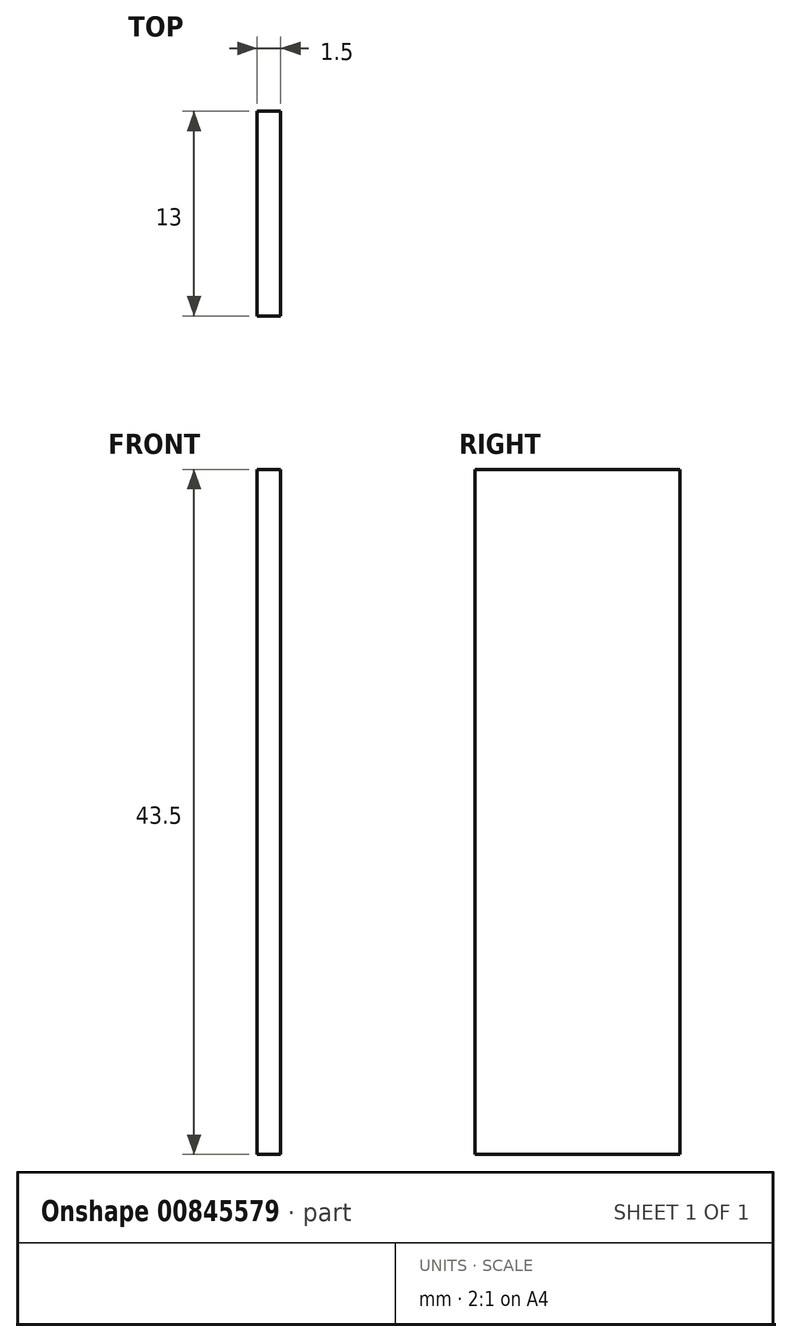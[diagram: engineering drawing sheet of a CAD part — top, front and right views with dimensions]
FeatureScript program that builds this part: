
annotation { "Feature Type Name" : "Feature", "Feature Type Description" : "" }
export const myFeature = defineFeature(function(context is Context, id is Id, definition is map)
    precondition{}
    {
        {
            var Q0;
            Q0=qCreatedBy(makeId("Right.planeOp"),FACE);
            var sketch = newSketch(context, id + "F0", { "sketchPlane" : qUnion([Q0])});
            skLineSegment(sketch, "E0.bottom", {"start": v(-6.5, 21.75) * mm, "end": v(6.5, 21.75) * mm});
            skLineSegment(sketch, "E0.top", {"start": v(-6.5, -21.75) * mm, "end": v(6.5, -21.75) * mm});
            skLineSegment(sketch, "E0.left", {"start": v(-6.5, 21.75) * mm, "end": v(-6.5, -21.75) * mm});
            skLineSegment(sketch, "E0.right", {"start": v(6.5, 21.75) * mm, "end": v(6.5, -21.75) * mm});
            skPoint(sketch, "E0.middle", {"position": v(0, 0) * mm});
            skSolve(sketch);
        }
        {
            var Q0;
            Q0=makeQuery(id+"F0.imprint","IMPRINT",FACE,{"disambiguationData":[TD([[makeQuery(id+"F0.imprint","IMPRINT",EDGE,{"derivedFrom":sQuery(id+"F0.wireOp",EDGE,"E0.bottom")}),-1.0]])]});
            extrude(context, id + "F1", {"entities" : qUnion([Q0]), "depth" : 1.5 * mm, "offsetDistance" : 25 * mm});
        }
    });
